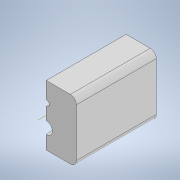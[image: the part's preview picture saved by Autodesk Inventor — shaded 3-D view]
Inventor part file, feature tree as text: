
AUTODESK INVENTOR PART (.ipt)
format: ipt  version: 2022 (Build 260153000, 153)  size: 21,305,856 bytes
history: native  units: mm
features: sketch x7, projected_geometry x4, other x3, extrude x3, move_body x2, revolve x2, hole x2, direct_edit x1, fillet x1, boolean_combine x1, sweep x1, pattern_circular x1, thicken_offset x1
ambient origin geometry x8: Origin, YZ Plane, XZ Plane, XY Plane, X Axis, Y Axis, Z Axis, Center Point
bodies: Solid1 (feature_tree), Solid2 (feature_tree), Solid3 (feature_tree), Solid4 (feature_tree)
feature tree (29):
  other  "MeshFeature1"
  direct_edit  "Direct Edit1"
  move_body  "Move Body1"
  move_body  "Move Body2"
  sketch  "Sketch1"  dims[d0=6.7mm d1=10.0mm d2=10.0mm d3=1.805mm d4=0.088mm d5=0.0mm d6=40.0mm]
  extrude  "Extrusion1"  Depth=10.0mm TaperAngle=0.0deg
  fillet  "Fillet1"  Radius=40.0mm
  extrude  "Extrusion2"  Depth=5.0mm
  boolean_combine  "Combine1"
  revolve  "Revolution1"  [1 undecoded]
  sweep  "Sweep1"
  extrude  "Extrusion3"  Depth=4.0mm TaperAngle=0.0deg
  other  "Work Axis1"
  pattern_circular  "Circular Pattern1"  Angle=90.0deg  [1 undecoded]
  thicken_offset  "Thicken1"
  hole  "Hole1"  [1 undecoded]
  hole  "Hole2"  [1 undecoded]
  revolve  "Revolution2"  [1 undecoded]
  sketch  "Sketch2"  dims[d7=0.0mm d8=-0.176mm d9=0.0mm d10=135.0deg d11=5.0mm]
  projected_geometry  "Projected Loop1"
  sketch  "Sketch3"  dims[d12=5.0mm d13=4.0mm]
  sketch  "Sketch4"  dims[d14=5.0mm d15=3.0mm]
  projected_geometry  "Projected Loop2"
  sketch  "Sketch5"  dims[d16=4.0mm d17=40.0mm d18=0.0mm]
  projected_geometry  "Projected Loop3"
  sketch  "Sketch6"  dims[d19=4.0mm]
  projected_geometry  "Projected Loop4"
  sketch  "Sketch7"  dims[d20=4.0mm d21=0.0mm d22=90.0deg d23=8.0mm d24=0.0mm d25=0.0mm d26=4.0mm d27=0.0mm d28=20.0mm d29=360.0deg d31=2.0mm d32=2.0mm d33=3.4mm d34=6.0mm d35=6.3mm d36=2.0mm d37=90.0deg d38=14.0mm d39=0.0mm d42=4.0mm d43=6.0mm d44=6.3mm d45=2.0mm d46=90.0deg d47=14.0mm d48=0.0mm d49=45.0deg d50=90.0deg d51=15.358897mm]
  other  "Scale1"
note: 5 required parameter values undecoded (feature->parameter linkage not recoverable at this tier; creation-order binding heuristic only, values carry confidence <= 0.55)